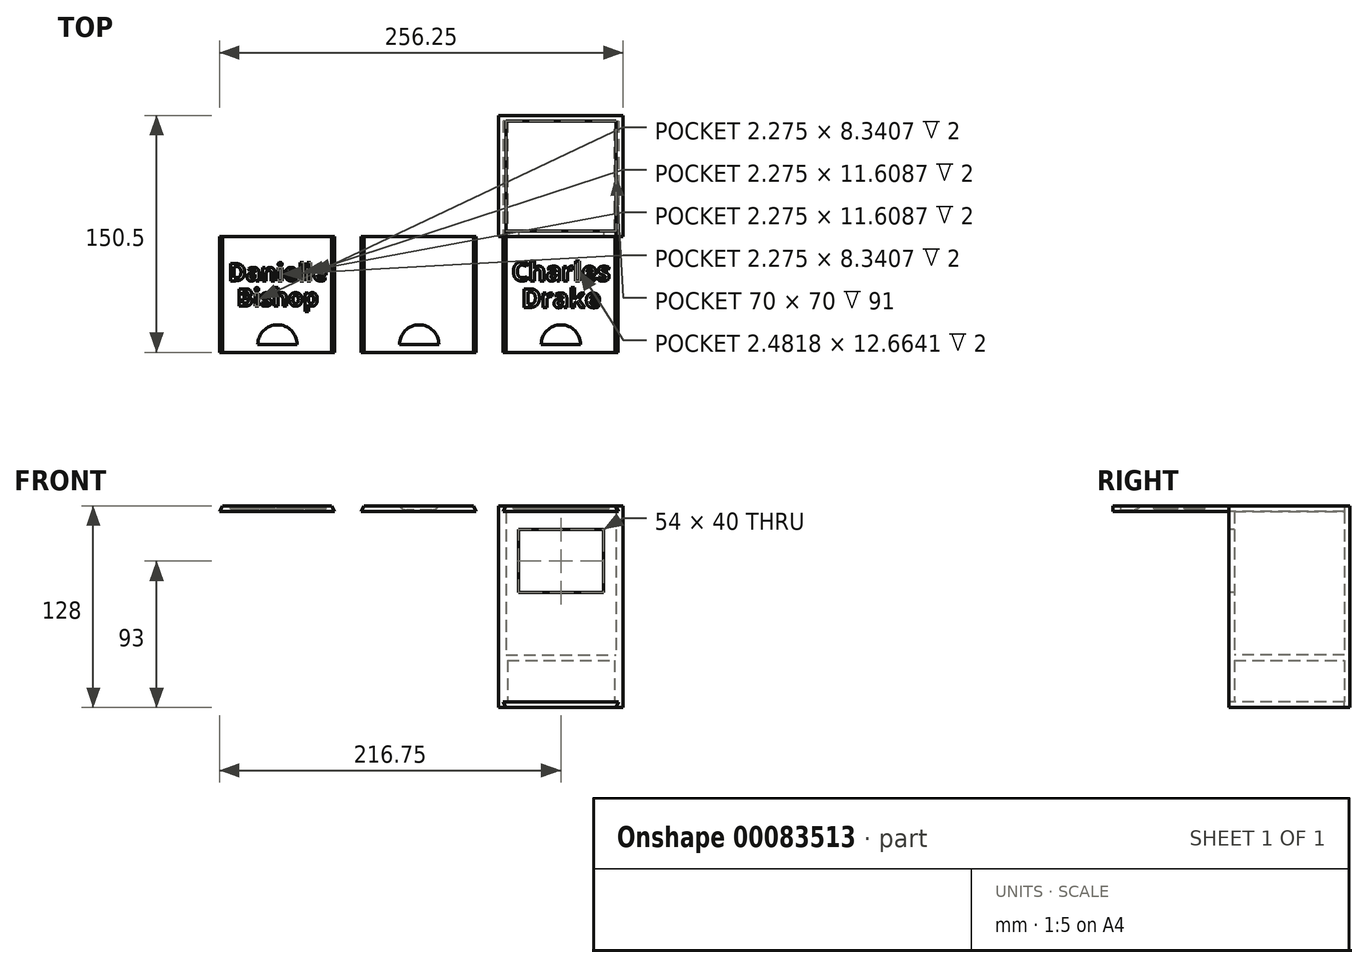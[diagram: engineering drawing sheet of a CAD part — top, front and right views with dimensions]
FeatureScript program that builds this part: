
annotation { "Feature Type Name" : "Feature", "Feature Type Description" : "" }
export const myFeature = defineFeature(function(context is Context, id is Id, definition is map)
    precondition{}
    {
        {
            var Q0;
            Q0=qCreatedBy(makeId("Top.planeOp"),FACE);
            var sketch = newSketch(context, id + "F0", { "sketchPlane" : qUnion([Q0])});
            skLineSegment(sketch, "E0.bottom", {"start": v(-38.5, 38.5) * mm, "end": v(38.5, 38.5) * mm});
            skLineSegment(sketch, "E0.top", {"start": v(-38.5, -38.5) * mm, "end": v(38.5, -38.5) * mm});
            skLineSegment(sketch, "E0.left", {"start": v(-38.5, 38.5) * mm, "end": v(-38.5, -38.5) * mm});
            skLineSegment(sketch, "E0.right", {"start": v(38.5, 38.5) * mm, "end": v(38.5, -38.5) * mm});
            skPoint(sketch, "E0.middle", {"position": v(0, 0) * mm});
            skSolve(sketch);
        }
        {
            var Q0;
            Q0=makeQuery(id+"F0.imprint","IMPRINT",FACE,{"disambiguationData":[TD([[makeQuery(id+"F0.imprint","IMPRINT",EDGE,{"derivedFrom":sQuery(id+"F0.wireOp",EDGE,"E0.bottom")}),-1.0]])]});
            extrude(context, id + "F1", {"entities" : qUnion([Q0]), "depth" : 98 * mm});
        }
        {
            var Q0;
            Q0=makeQuery(id+"F1.opExtrude","CAP_FACE",FACE,{"disambiguationData":[OSD([sQuery(id+"F0.wireOp",EDGE,"E0.bottom"),sQuery(id+"F0.wireOp",EDGE,"E0.top"),sQuery(id+"F0.wireOp",EDGE,"E0.left"),sQuery(id+"F0.wireOp",EDGE,"E0.right")])],"isStart":false});
            shell(context, id + "F2", {"entities" : qUnion([Q0]), "thickness" : 3.5 * mm});
        }
        {
            var Q0;
            Q0=makeQuery(id+"F1.opExtrude","SWEPT_FACE",FACE,{"disambiguationData":[OSD([sQuery(id+"F0.wireOp",EDGE,"E0.top")])]});
            var sketch = newSketch(context, id + "F3", { "sketchPlane" : qUnion([Q0])});
            skLineSegment(sketch, "E1", {"start": v(-38.5, 107.19) * mm, "end": v(38.5, 107.19) * mm, "construction": true});
            skLineSegment(sketch, "E2.bottom", {"start": v(-27, 83) * mm, "end": v(27, 83) * mm});
            skLineSegment(sketch, "E2.top", {"start": v(-27, 43) * mm, "end": v(27, 43) * mm});
            skLineSegment(sketch, "E2.left", {"start": v(-27, 83) * mm, "end": v(-27, 43) * mm});
            skLineSegment(sketch, "E2.right", {"start": v(27, 83) * mm, "end": v(27, 43) * mm});
            skLineSegment(sketch, "E3", {"start": v(0, 98) * mm, "end": v(0, 0) * mm, "construction": true});
            skLineSegment(sketch, "E4", {"start": v(0, 83) * mm, "end": v(0, 43) * mm, "construction": true});
            skSolve(sketch);
        }
        {
            var Q0;
            Q0=makeQuery(id+"F3.imprint","IMPRINT",FACE,{"disambiguationData":[TD([[makeQuery(id+"F3.imprint","IMPRINT",EDGE,{"derivedFrom":sQuery(id+"F3.wireOp",EDGE,"E2.bottom")}),-1.0]])]});
            extrude(context, id + "F4", {"entities" : qUnion([Q0]), "operationType" : NewBodyOperationType.REMOVE, "endBound" : BoundingType.UP_TO_NEXT, "oppositeDirection" : true, "depth" : 25 * mm});
        }
        {
            var Q0;
            Q0=makeQuery(id+"F1.opExtrude","SWEPT_FACE",FACE,{"disambiguationData":[OSD([sQuery(id+"F0.wireOp",EDGE,"E0.top")])]});
            var sketch = newSketch(context, id + "F5", { "sketchPlane" : qUnion([Q0])});
            skLineSegment(sketch, "E5", {"start": v(-35, 98) * mm, "end": v(-35, 0) * mm, "construction": true});
            skLineSegment(sketch, "E6", {"start": v(35, 98) * mm, "end": v(35, 0) * mm, "construction": true});
            skLineSegment(sketch, "E7", {"start": v(-38.5, 94.5) * mm, "end": v(38.5, 94.5) * mm, "construction": true});
            skLineSegment(sketch, "E8", {"start": v(-36.75, 94.5) * mm, "end": v(-36.75, 98) * mm, "construction": true});
            skLineSegment(sketch, "E9", {"start": v(36.75, 94.5) * mm, "end": v(36.75, 98) * mm, "construction": true});
            skPoint(sketch, "E9.endSnap0", {"position": v(0, 98) * mm});
            skLineSegment(sketch, "E10", {"start": v(-35, 98) * mm, "end": v(-36.75, 94.5) * mm});
            skLineSegment(sketch, "E11", {"start": v(-35, 94.5) * mm, "end": v(-35, 98) * mm});
            skLineSegment(sketch, "E12", {"start": v(35, 98) * mm, "end": v(36.75, 94.5) * mm});
            skLineSegment(sketch, "E13", {"start": v(35, 94.5) * mm, "end": v(35, 98) * mm});
            skLineSegment(sketch, "E14", {"start": v(-36.75, 94.5) * mm, "end": v(36.75, 94.5) * mm});
            skSolve(sketch);
        }
        {
            var Q0;
            {var subQ0=sQuery(id+"F5.wireOp",EDGE,"E11");Q0=makeQuery(id+"F5.imprint","IMPRINT",FACE,{"disambiguationData":[TD([[makeQuery(id+"F5.imprint","IMPRINT",EDGE,{"derivedFrom":subQ0}),-1.0]])]});}
            var Q1;
            {var subQ0=sQuery(id+"F5.wireOp",EDGE,"E12");Q1=makeQuery(id+"F5.imprint","IMPRINT",FACE,{"disambiguationData":[TD([[makeQuery(id+"F5.imprint","IMPRINT",EDGE,{"derivedFrom":subQ0}),-1.0]])]});}
            var Q2;
            {var subQ0=sQuery(id+"F5.wireOp",EDGE,"E10");Q2=makeQuery(id+"F5.imprint","IMPRINT",FACE,{"disambiguationData":[TD([[makeQuery(id+"F5.imprint","IMPRINT",EDGE,{"derivedFrom":subQ0}),1.0]])]});}
            extrude(context, id + "F6", {"entities" : qUnion([Q0, Q1, Q2]), "operationType" : NewBodyOperationType.REMOVE, "oppositeDirection" : true, "depth" : (77 - 3.5) * mm});
        }
        {
            var Q0;
            Q0=makeQuery(id+"F1.opExtrude","SWEPT_FACE",FACE,{"disambiguationData":[OSD([sQuery(id+"F0.wireOp",EDGE,"E0.right")])]});
            extrude(context, id + "F7", {"entities" : qUnion([Q0]), "operationType" : NewBodyOperationType.ADD, "depth" : 1 * mm});
        }
        {
            var Q0;
            Q0=makeQuery(id+"F1.opExtrude","SWEPT_FACE",FACE,{"disambiguationData":[OSD([sQuery(id+"F0.wireOp",EDGE,"E0.left")])]});
            extrude(context, id + "F8", {"entities" : qUnion([Q0]), "operationType" : NewBodyOperationType.ADD, "depth" : 1 * mm});
        }
        {
            var Q0;
            {var subQ0=sQuery(id+"F0.wireOp",EDGE,"E0.left");var subQ1=sQuery(id+"F0.wireOp",EDGE,"E0.right");Q0=makeQuery(id+"F8.boolean.opBoolean","MERGE",FACE,{"derivedFrom":[makeQuery(id+"F7.boolean.opBoolean","MERGE",FACE,{"derivedFrom":[makeQuery(id+"F1.opExtrude","CAP_FACE",FACE,{"disambiguationData":[OSD([sQuery(id+"F0.wireOp",EDGE,"E0.bottom"),sQuery(id+"F0.wireOp",EDGE,"E0.top"),subQ0,subQ1])],"isStart":true}),makeQuery(id+"F7.opExtrude","SWEPT_FACE",FACE,{"disambiguationData":[OSD([subQ1]),TDD([makeQuery(id+"F1.opExtrude","CAP_EDGE",EDGE,{"disambiguationData":[OSD([subQ1])],"isStart":true})])]})]}),makeQuery(id+"F8.opExtrude","SWEPT_FACE",FACE,{"disambiguationData":[OSD([subQ0]),TDD([makeQuery(id+"F1.opExtrude","CAP_EDGE",EDGE,{"disambiguationData":[OSD([subQ0])],"isStart":true})])]})]});}
            extrude(context, id + "F9", {"entities" : qUnion([Q0]), "operationType" : NewBodyOperationType.ADD, "depth" : 30 * mm});
        }
        {
            var Q0;
            Q0=makeQuery(id+"F9.opExtrude","CAP_FACE",FACE,{"disambiguationData":[OSD([sQuery(id+"F0.wireOp",EDGE,"E0.bottom"),sQuery(id+"F0.wireOp",EDGE,"E0.top"),sQuery(id+"F0.wireOp",EDGE,"E0.left"),sQuery(id+"F0.wireOp",EDGE,"E0.right")])],"isStart":false});
            var sketch = newSketch(context, id + "F10", { "sketchPlane" : qUnion([Q0])});
            skLineSegment(sketch, "E15", {"start": v(-34, 38.5) * mm, "end": v(-34, -38.5) * mm, "construction": true});
            skLineSegment(sketch, "E16", {"start": v(34, 38.5) * mm, "end": v(34, -38.5) * mm, "construction": true});
            skLineSegment(sketch, "E17", {"start": v(-39.5, -35) * mm, "end": v(39.5, -35) * mm, "construction": true});
            skLineSegment(sketch, "E18", {"start": v(-34, 38.5) * mm, "end": v(-34, -35) * mm});
            skLineSegment(sketch, "E19", {"start": v(-34, -35) * mm, "end": v(34, -35) * mm});
            skLineSegment(sketch, "E20", {"start": v(34, -35) * mm, "end": v(34, 38.5) * mm});
            skLineSegment(sketch, "E21", {"start": v(-34, 35) * mm, "end": v(34, 35) * mm});
            skSolve(sketch);
        }
        {
            var Q0;
            {var subQ0=sQuery(id+"F10.wireOp",EDGE,"E19");Q0=makeQuery(id+"F10.imprint","IMPRINT",FACE,{"disambiguationData":[TD([[makeQuery(id+"F10.imprint","IMPRINT",EDGE,{"derivedFrom":subQ0}),1.0]])]});}
            extrude(context, id + "F11", {"entities" : qUnion([Q0]), "operationType" : NewBodyOperationType.REMOVE, "oppositeDirection" : true, "depth" : 30 * mm});
        }
        {
            var Q0;
            {var subQ0=sQuery(id+"F0.wireOp",EDGE,"E0.right");var subQ1=sQuery(id+"F0.wireOp",EDGE,"E0.left");var subQ2=sQuery(id+"F0.wireOp",EDGE,"E0.top");Q0=makeQuery(id+"F9.boolean.opBoolean","MERGE",FACE,{"derivedFrom":[makeQuery(id+"F8.boolean.opBoolean","MERGE",FACE,{"derivedFrom":[makeQuery(id+"F7.boolean.opBoolean","MERGE",FACE,{"derivedFrom":[makeQuery(id+"F1.opExtrude","SWEPT_FACE",FACE,{"disambiguationData":[OSD([subQ2])]}),makeQuery(id+"F7.opExtrude","SWEPT_FACE",FACE,{"disambiguationData":[OSD([subQ2,subQ0])]})]}),makeQuery(id+"F8.opExtrude","SWEPT_FACE",FACE,{"disambiguationData":[OSD([subQ2,subQ1])]})]}),makeQuery(id+"F9.opExtrude","SWEPT_FACE",FACE,{"disambiguationData":[OSD([subQ2,subQ1,subQ0])]})]});}
            var sketch = newSketch(context, id + "F12", { "sketchPlane" : qUnion([Q0])});
            skLineSegment(sketch, "E22", {"start": v(-39.5, -26.5) * mm, "end": v(39.5, -26.5) * mm, "construction": true});
            skLineSegment(sketch, "E23", {"start": v(-35, -30) * mm, "end": v(-35, -26.5) * mm, "construction": true});
            skLineSegment(sketch, "E24", {"start": v(35, -30) * mm, "end": v(35, -26.5) * mm, "construction": true});
            skLineSegment(sketch, "E25", {"start": v(-36.75, -30) * mm, "end": v(-36.75, -26.5) * mm, "construction": true});
            skLineSegment(sketch, "E26", {"start": v(36.75, -30) * mm, "end": v(36.75, -26.5) * mm, "construction": true});
            skLineSegment(sketch, "E27", {"start": v(-35, -30) * mm, "end": v(-36.75, -26.5) * mm});
            skLineSegment(sketch, "E28", {"start": v(36.75, -26.5) * mm, "end": v(35, -30) * mm});
            skLineSegment(sketch, "E29", {"start": v(-36.75, -26.5) * mm, "end": v(36.75, -26.5) * mm});
            skSolve(sketch);
        }
        {
            var Q0;
            {var subQ0=sQuery(id+"F12.wireOp",EDGE,"E27");Q0=makeQuery(id+"F12.imprint","IMPRINT",FACE,{"disambiguationData":[TD([[makeQuery(id+"F12.imprint","IMPRINT",EDGE,{"derivedFrom":subQ0}),-1.0]])]});}
            extrude(context, id + "F13", {"entities" : qUnion([Q0]), "operationType" : NewBodyOperationType.REMOVE, "oppositeDirection" : true, "depth" : (77 - 3.5) * mm});
        }
        {
            var Q0;
            {var subQ0=sQuery(id+"F0.wireOp",EDGE,"E0.right");var subQ1=sQuery(id+"F0.wireOp",EDGE,"E0.left");var subQ2=sQuery(id+"F0.wireOp",EDGE,"E0.top");Q0=makeQuery(id+"F9.boolean.opBoolean","MERGE",FACE,{"derivedFrom":[makeQuery(id+"F8.boolean.opBoolean","MERGE",FACE,{"derivedFrom":[makeQuery(id+"F7.boolean.opBoolean","MERGE",FACE,{"derivedFrom":[makeQuery(id+"F1.opExtrude","SWEPT_FACE",FACE,{"disambiguationData":[OSD([subQ2])]}),makeQuery(id+"F7.opExtrude","SWEPT_FACE",FACE,{"disambiguationData":[OSD([subQ2,subQ0])]})]}),makeQuery(id+"F8.opExtrude","SWEPT_FACE",FACE,{"disambiguationData":[OSD([subQ2,subQ1])]})]}),makeQuery(id+"F9.opExtrude","SWEPT_FACE",FACE,{"disambiguationData":[OSD([subQ2,subQ1,subQ0])]})]});}
            var sketch = newSketch(context, id + "F14", { "sketchPlane" : qUnion([Q0])});
            skLineSegment(sketch, "E30.0", {"start": v(35, 98) * mm, "end": v(36.75, 94.5) * mm});
            skLineSegment(sketch, "E30.1", {"start": v(-36.75, 94.5) * mm, "end": v(36.75, 94.5) * mm});
            skLineSegment(sketch, "E30.2", {"start": v(-35, 98) * mm, "end": v(-36.75, 94.5) * mm});
            skLineSegment(sketch, "E30.3", {"start": v(-35, 98) * mm, "end": v(35, 98) * mm});
            skLineSegment(sketch, "E31", {"start": v(34.5, 98) * mm, "end": v(36.25, 94.5) * mm});
            skSolve(sketch);
        }
        {
            var Q0;
            {var subQ0=sQuery(id+"F14.wireOp",EDGE,"E30.2");Q0=makeQuery(id+"F14.imprint","IMPRINT",FACE,{"disambiguationData":[TD([[makeQuery(id+"F14.imprint","IMPRINT",EDGE,{"derivedFrom":subQ0}),1.0]])]});}
            extrude(context, id + "F15", {"entities" : qUnion([Q0]), "depth" : (77 - 3.5) * mm});
        }
        {
            var Q0;
            Q0=makeQuery(id+"F15.opExtrude","SWEPT_FACE",FACE,{"disambiguationData":[OSD([sQuery(id+"F14.wireOp",EDGE,"E30.3")])]});
            var sketch = newSketch(context, id + "F16", { "sketchPlane" : qUnion([Q0])});
            skLineSegment(sketch, "E32", {"start": v(-35, -107) * mm, "end": v(-35, -107) * mm});
            skArc(sketch, "E33", {"start": v(12.5, -107) * mm, "mid": v(0, -94.5) * mm, "end": v(-12.5, -107) * mm});
            skLineSegment(sketch, "E34", {"start": v(12.5, -107) * mm, "end": v(-12.5, -107) * mm});
            skSolve(sketch);
        }
        {
            var Q0;
            Q0=makeQuery(id+"F16.imprint","IMPRINT",FACE,{"disambiguationData":[TD([[makeQuery(id+"F16.imprint","IMPRINT",EDGE,{"derivedFrom":sQuery(id+"F16.wireOp",EDGE,"E33")}),1.0]])]});
            extrude(context, id + "F17", {"entities" : qUnion([Q0]), "operationType" : NewBodyOperationType.REMOVE, "oppositeDirection" : true, "depth" : 2.5 * mm});
        }
        {
            var Q0;
            Q0=makeQuery(id+"F17.boolean.opBoolean","COPY",EDGE,{"derivedFrom":makeQuery(id+"F17.opExtrude","CAP_EDGE",EDGE,{"disambiguationData":[OSD([sQuery(id+"F16.wireOp",EDGE,"E33")])],"isStart":false})});
            fillet(context, id + "F18", {"entities" : qUnion([Q0]), "radius" : 5 * mm, "tangentPropagation" : true, "allowEdgeOverflow" : false});
        }
        {
            var Q0;
            Q0=makeQuery(id+"F15.opExtrude","SWEPT_BODY",BODY,{"disambiguationData":[OSD([sQuery(id+"F14.wireOp",EDGE,"E30.0"),sQuery(id+"F14.wireOp",EDGE,"E30.1"),sQuery(id+"F14.wireOp",EDGE,"E30.2"),sQuery(id+"F14.wireOp",EDGE,"E30.3")])]});
            var Q1;
            {var subQ0=sQuery(id+"F0.wireOp",EDGE,"E0.left");Q1=makeQuery(id+"F9.boolean.opBoolean","MERGE",FACE,{"derivedFrom":[makeQuery(id+"F8.opExtrude","CAP_FACE",FACE,{"disambiguationData":[OSD([subQ0])],"isStart":false}),makeQuery(id+"F9.opExtrude","SWEPT_FACE",FACE,{"disambiguationData":[OSD([subQ0])]})]});}
            transform(context, id + "F19", {"entities" : qUnion([Q0]), "transformType" : TransformType.TRANSLATION_DISTANCE, "transformDirection" : qUnion([Q1]), "distance" : 90 * mm, "makeCopy" : true});
        }
        {
            var Q0;
            Q0=makeQuery(id+"F15.opExtrude","SWEPT_FACE",FACE,{"disambiguationData":[OSD([sQuery(id+"F14.wireOp",EDGE,"E30.3")])]});
            var sketch = newSketch(context, id + "F20", { "sketchPlane" : qUnion([Q0])});
            skLineSegment(sketch, "E35", {"start": v(-0.25, -38.5) * mm, "end": v(-0.25, -112) * mm, "construction": true});
            skText(sketch, "E36", { "text": "Charles", "fontName": "OpenSans-Bold.ttf"});
            skText(sketch, "E37", { "text": "Drake", "fontName": "OpenSans-Bold.ttf"});
            const initialGuessF20  = {"E36": [-0.03115, -0.0665, 1, 0, 0.012], "E37": [-0.02497, -0.0835, 1, 0, 0.012]};
            skSetInitialGuess(sketch, initialGuessF20);
            skSolve(sketch);
        }
        {
            var Q0;
            Q0 = qSketchRegion(id + "F20", true);
            extrude(context, id + "F21", {"entities" : qUnion([Q0]), "operationType" : NewBodyOperationType.REMOVE, "oppositeDirection" : true, "depth" : 2 * mm});
        }
        {
            var Q0;
            Q0=makeQuery(id+"F19.opPattern","COPY",BODY,{"derivedFrom":makeQuery(id+"F15.opExtrude","SWEPT_BODY",BODY,{"disambiguationData":[OSD([sQuery(id+"F14.wireOp",EDGE,"E30.1"),sQuery(id+"F14.wireOp",EDGE,"E30.2"),sQuery(id+"F14.wireOp",EDGE,"E30.3"),sQuery(id+"F14.wireOp",EDGE,"E31")])]}),"instanceName":"1"});
            var Q1;
            {var subQ0=sQuery(id+"F0.wireOp",EDGE,"E0.left");Q1=makeQuery(id+"F9.boolean.opBoolean","MERGE",FACE,{"derivedFrom":[makeQuery(id+"F8.opExtrude","CAP_FACE",FACE,{"disambiguationData":[OSD([subQ0])],"isStart":false}),makeQuery(id+"F9.opExtrude","SWEPT_FACE",FACE,{"disambiguationData":[OSD([subQ0])]})]});}
            transform(context, id + "F22", {"entities" : qUnion([Q0]), "transformType" : TransformType.TRANSLATION_DISTANCE, "transformDirection" : qUnion([Q1]), "distance" : 90 * mm, "makeCopy" : true});
        }
        {
            var Q0;
            Q0=makeQuery(id+"F22.opPattern","COPY",FACE,{"derivedFrom":makeQuery(id+"F19.opPattern","COPY",FACE,{"derivedFrom":makeQuery(id+"F15.opExtrude","SWEPT_FACE",FACE,{"disambiguationData":[OSD([sQuery(id+"F14.wireOp",EDGE,"E30.3")])]}),"instanceName":"1"}),"instanceName":"1"});
            var sketch = newSketch(context, id + "F23", { "sketchPlane" : qUnion([Q0])});
            skLineSegment(sketch, "E38", {"start": v(-180.25, -38.5) * mm, "end": v(-180.25, -112) * mm, "construction": true});
            skText(sketch, "E39", { "text": "Danielle", "fontName": "OpenSans-Bold.ttf"});
            skText(sketch, "E40", { "text": "Bishop", "fontName": "OpenSans-Bold.ttf"});
            const initialGuessF23  = {"E39": [-0.21123, -0.0665, 1, 0, 0.011], "E40": [-0.20575, -0.0825, 1, 0, 0.011]};
            skSetInitialGuess(sketch, initialGuessF23);
            skSolve(sketch);
        }
        {
            var Q0;
            Q0 = qSketchRegion(id + "F23", true);
            extrude(context, id + "F24", {"entities" : qUnion([Q0]), "operationType" : NewBodyOperationType.REMOVE, "oppositeDirection" : true, "depth" : 2 * mm});
        }
    });
